# Revit family: IS_Ceraplan_BD332_BIM_DE
name_source: partatom
category: Plumbing Fixtures
units: mm (PartAtom-declared; Revit-internal decimal feet)

## family parameters
Always vertical = No
Cut with Voids When Loaded = No
OmniClass Number = 23.45.55.17
OmniClass Title = Mixing Faucets
Part Type = Normal
Room Calculation Point = No
Round Connector Dimension = Use Diameter
Shared = No
Work Plane-Based = No

## types (1)
- BD332AA - Ceraplan Single lever kitchen mixer Rim-Montedwith high attached spout pull- out spray 1 function Blue Start - Chrome
    Accesoires = https://www.idealstandard.de
    Accessories = https://www.idealstandard.de
    Afmetingen = 50 x 256 x 210 mm
    AfstandsEenheid = Millimeter
    Afwerking = Chrom
    AreaUnits = millimetres
    Artikelnummer = BD332AA
    Artikelomschrijving = Ceraplan Einhebel-Küchenmischer Wannenrand mit hochgesetztem Auslauf Ausziehbrause 1 Funktion Blue Start
    Artikelreferentie = BD332AA
    BIMObjectName = IS_IdealStandard_Sinktaps_Ceraplan_BD332
    BIMobject category = Taps & Mixers
    BIMobject category code = sanitary-taps-mixers
    BIMobject main category = Sanitary
    BIMobject main category code = sanitary
    BarCode = 3800861104933
    Bedieningkraan = einzelne Leber
    Beschrijvinggarantie = Herstellergarantie
    BimObjectNaam = IS_IdealStandard_Sinktaps_Ceraplan_BD332
    Brand = Ideal Standard
    Brand url = http://www.idealstandard.de
    Breedte = 50.017061
    BrutoGewicht = 0
    Category = Taps & Mixer
    Color = Chrome
    ConnectionType = Plumbing
    CurrencyUnit = €
    CurrentRevision = 1
    Date of publishing = 25/03/2022
    Description = Ceraplan Einhebel-Küchenmischer Wannenrand mit hochgesetztem Auslauf Ausziehbrause 1 Funktion Blue Start
    Diepte = 256 mm
    DurationUnit = Jahre
    DuurEenheid = Jahre
    Edition number = 1
    Eigenschappen = Einhebel-Küchenmischer Wannenrand mit hochgesetztem Auslauf Ausziehbrause 1 Funktion Blue Start
    FaucetFunction = Kitchen Mixer
    FaucetOperation = Single Lever Kitchen mixer
    FaucetTopDescription = Single Lever Kitchen mixer
    FaucetType = Kitchen Mixer
    Features = Einhebel-Küchenmischer Wannenrand mit hochgesetztem Auslauf Ausziehbrause 1 Funktion Blue Start
    Finish = Chrome
    Functiekraanwerk = Einhebel-Küchenmischer
    GTIN code = https://3800861104933
    Garantieonderdelen = 5
    Garantieunits = Jahre
    GemaaktOp = 25/03/2022
    Help = https://www.idealstandard.de
    Hoogte = 210.11693
    Hulp = https://www.idealstandard.de
    IFC Classification = Sanitary Terminal
    IfcExportAs = IfcValveType
    IfcExportType = FAUCET
    Installatieinstructies = https://www.idealstandard.de
    Installation instructions = https://www.idealstandard.de
    InstallationInstructions = https://www.idealstandard.de
    Klepmechanisme = Einhebel
    Kleur = Chrom
    Lengte = 256 mm
    LinearUnits = millimeters
    MainColor = Chrome
    MaintenanceInformation = https://www.idealstandard.de
    Manufacturer = Ideal Standard
    Manufacturer name = Ideal Standard
    ManufacturerURL = https://www.idealstandard.de
    Materiaal = Messing
    Material = Messing
    Material main = Messing
    Merk = Ideal Standard
    Model = BD332AA
    ModelNumber = BD332AA
    ModelReference = Ceraplan Single lever kitchen mixer Rim-Montedwith high attached spout pull- out spray 1 function Blue Start
    NBS Reference Code = 45-35-70/345
    NBS Reference Description = Water supply fittings for sinks
    Name = Sinktaps_Ceraplan_BD332_IdealStandard
    NettWeight = 2,8 Kg
    Nettogewicht = 0
    NominalDepth = 256 mm
    NominalHeight = 210 mm
    NominalLength = 256 mm
    NominalWidth = 50 mm
    Normen = Sinktaps_Ceraplan_BD332_IdealStandard
    OmniClass Code = 23-31 11 00
    OmniClass Description = Faucets
    OppervlakteEenheid = Millimeter
    Product Guid = 8fab6491-1b78-4dfe-a348-7cf8bf6928da
    Product SKU = BD332
    Product certification = https://www.idealstandard.de
    Product data url = https://bimobject.com
    Product family = CERAPLAN
    Product group = Kitchen Mixers
    Product name = Ceraplan Single lever kitchen mixer Rim-Montedwith high attached spout pull- out spray 1 function Blue Start
    Product url = https://www.idealstandard.de
    ProductInformation = https://www.idealstandard.de
    ProductSoort = Küchenmischer
    Productinformatie = https://www.idealstandard.de
    QR code = http://bimobject.com
    Revisie = 1
    Shape = cylindrical
    Size = 50 x 256 x 210 mm
    Space = Internal
    SpareParts = https://www.idealstandard.de
    Technical description = https://www.idealstandard.de
    Telefoonnummer = (0228) 521-580
    Testdruk = 10 bar
    Toepassing = Küchenmischer
    Typekraanwerk = Einhebel-Küchenmischer
    UNSPSC Code = 301815
    URL = https://www.idealstandard.de
    Uniclass 1.4 Code = L725111
    Uniclass 1.4 Description = Mixer taps
    Uniclass 2.0 Code = PR-35-79-79
    Uniclass 2.0 Description = Sink Water Supply Fittings
    Uniclass 2015 Code = Pr_40_20_87_84
    Uniclass 2015 Name = Sink taps
    Uniclass2015Beschrijving = Sink taps
    Uniclass2015Code = Pr_40_20_87_84
    Uniclass2015Referentie = Pr_40_20_87_84
    Uniclass2015Title = Sink taps
    Uniclass2015Version = v1.25
    Uniformat II Code = PR-35-79-79
    Uniformat II Description = SinkWaterSupplyFittings
    Urlproducent = https://www.idealstandard.de
    ValutaEenheid = Euro
    Versie = 1
    Version = 1
    Vervangingskosten = 0
    VolumeUnits = Litres
    Volumeunits = Liter
    Vorm = zylindrisch
    WRASURL = https://www.wrasapprovals.co.uk
    WarrantyDescription = manufacturer warranty
    WarrantyDurationParts = 5
    WarrantyDurationUnit = Years
    Wisselstukken = https://www.idealstandard.de
    Youtube clip = https://www.youtube.com

## geometry (parser evidence)
native form markers: Sweep x2
no freeform markers — native parametric forms only
